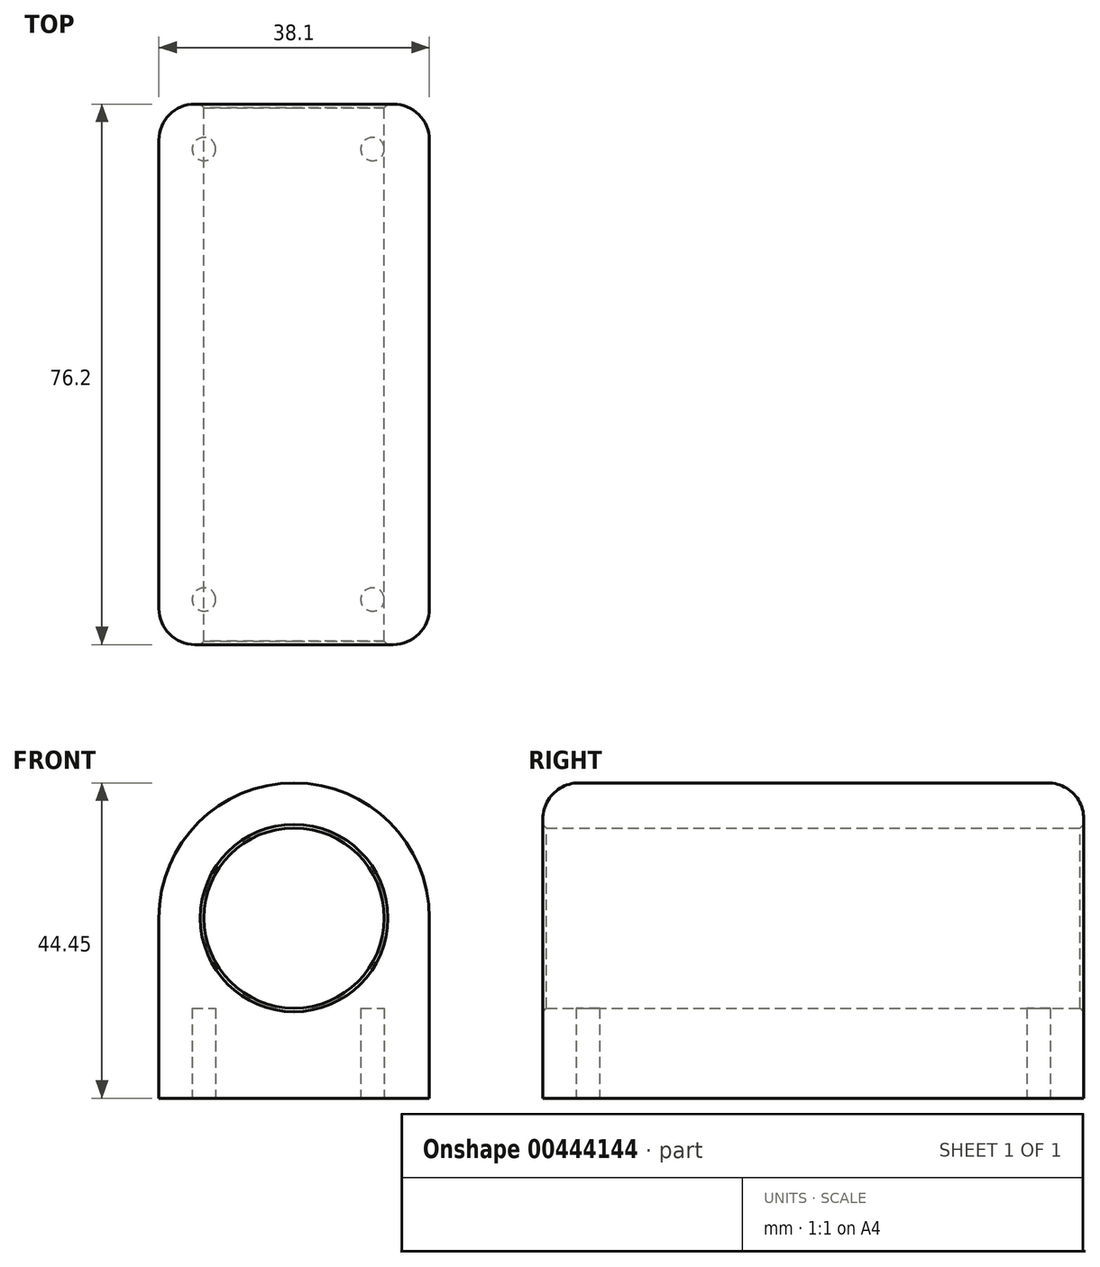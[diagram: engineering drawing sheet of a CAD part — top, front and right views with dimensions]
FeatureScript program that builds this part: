
annotation { "Feature Type Name" : "Feature", "Feature Type Description" : "" }
export const myFeature = defineFeature(function(context is Context, id is Id, definition is map)
    precondition{}
    {
        {
            var Q0;
            Q0=qCreatedBy(makeId("Front.planeOp"),FACE);
            var sketch = newSketch(context, id + "F0", { "sketchPlane" : qUnion([Q0])});
            skArc(sketch, "E0", {"start": v(19.05, 0) * mm, "mid": v(0, 19.05) * mm, "end": v(-19.05, 0) * mm});
            skLineSegment(sketch, "E1.top", {"start": v(-19.05, -25.4) * mm, "end": v(19.05, -25.4) * mm});
            skLineSegment(sketch, "E1.left", {"start": v(-19.05, 0) * mm, "end": v(-19.05, -25.4) * mm});
            skLineSegment(sketch, "E1.right", {"start": v(19.05, 0) * mm, "end": v(19.05, -25.4) * mm});
            skCircle(sketch, "E2", {"center": v(0, 0) * mm, "radius": 12.7 * mm});
            skSolve(sketch);
        }
        {
            var Q0;
            Q0 = qSketchRegion(id + "F0", true);
            extrude(context, id + "F1", {"entities" : qUnion([Q0]), "endBound" : BoundingType.SYMMETRIC, "depth" : 76.2 * mm});
        }
        {
            var Q0;
            Q0=makeQuery(id+"F1.opExtrude","SWEPT_FACE",FACE,{"disambiguationData":[OSD([sQuery(id+"F0.wireOp",EDGE,"E1.top")])]});
            var sketch = newSketch(context, id + "F2", { "sketchPlane" : qUnion([Q0])});
            skCircle(sketch, "E3", {"center": v(-12.7, 31.75) * mm, "radius": 1.65 * mm});
            skCircle(sketch, "E4", {"center": v(11.05, 31.75) * mm, "radius": 1.65 * mm});
            skCircle(sketch, "E5", {"center": v(-12.7, -31.75) * mm, "radius": 1.65 * mm});
            skCircle(sketch, "E6", {"center": v(11.05, -31.75) * mm, "radius": 1.65 * mm});
            skSolve(sketch);
        }
        {
            var Q0;
            Q0 = qSketchRegion(id + "F2", true);
            extrude(context, id + "F3", {"entities" : qUnion([Q0]), "operationType" : NewBodyOperationType.REMOVE, "oppositeDirection" : true, "depth" : 12.7 * mm});
        }
        {
            var Q0;
            Q0=makeQuery(id+"F1.opExtrude","CAP_EDGE",EDGE,{"disambiguationData":[OSD([sQuery(id+"F0.wireOp",EDGE,"E0")])],"isStart":true});
            var Q1;
            Q1=makeQuery(id+"F1.opExtrude","CAP_EDGE",EDGE,{"disambiguationData":[OSD([sQuery(id+"F0.wireOp",EDGE,"E0")])],"isStart":false});
            fillet(context, id + "F4", {"entities" : qUnion([Q0, Q1]), "radius" : 5.08 * mm, "tangentPropagation" : true, "allowEdgeOverflow" : false});
        }
        {
            var Q0;
            Q0=makeQuery(id+"F1.opExtrude","CAP_EDGE",EDGE,{"disambiguationData":[OSD([sQuery(id+"F0.wireOp",EDGE,"E2")])],"isStart":true});
            var Q1;
            Q1=makeQuery(id+"F1.opExtrude","CAP_EDGE",EDGE,{"disambiguationData":[OSD([sQuery(id+"F0.wireOp",EDGE,"E2")])],"isStart":false});
            chamfer(context, id + "F5", {"entities" : qUnion([Q0, Q1]), "width" : 0.5 * mm, "tangentPropagation" : true});
        }
    });
